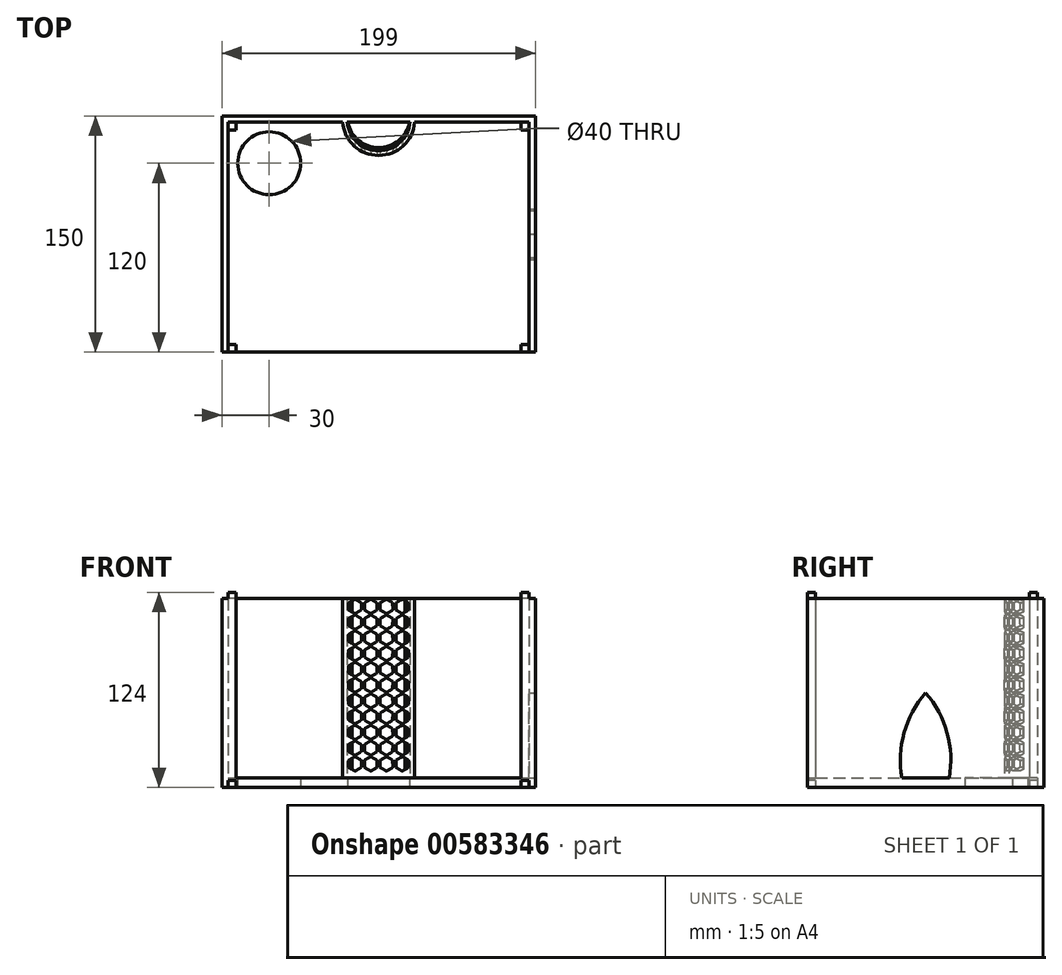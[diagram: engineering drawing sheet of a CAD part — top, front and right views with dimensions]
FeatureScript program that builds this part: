
annotation { "Feature Type Name" : "Feature", "Feature Type Description" : "" }
export const myFeature = defineFeature(function(context is Context, id is Id, definition is map)
    precondition{}
    {
        {
            var Q0;
            Q0=qCreatedBy(makeId("Top.planeOp"),FACE);
            var sketch = newSketch(context, id + "F0", { "sketchPlane" : qUnion([Q0])});
            skLineSegment(sketch, "E0.bottom", {"start": v(-99.5, 75) * mm, "end": v(99.5, 75) * mm});
            skLineSegment(sketch, "E0.left", {"start": v(-99.5, 75) * mm, "end": v(-99.5, -75) * mm});
            skLineSegment(sketch, "E0.right", {"start": v(99.5, 75) * mm, "end": v(99.5, -75) * mm});
            skPoint(sketch, "E0.middle", {"position": v(0, 0) * mm});
            skLineSegment(sketch, "E1.1", {"start": v(-95.5, 71) * mm, "end": v(-95.5, -70) * mm});
            skLineSegment(sketch, "E1.2", {"start": v(-95.5, 71) * mm, "end": v(95.4, 71) * mm});
            skLineSegment(sketch, "E1.3", {"start": v(95.4, 71) * mm, "end": v(95.4, -70) * mm});
            skLineSegment(sketch, "E2", {"start": v(0, -75) * mm, "end": v(0, -73) * mm});
            skPoint(sketch, "E2.endSnap0", {"position": v(0, -75) * mm});
            skPoint(sketch, "E3.end.orphan", {"position": v(95.5, 0) * mm});
            skLineSegment(sketch, "E4", {"start": v(-99.5, -75) * mm, "end": v(-95.5, -75) * mm});
            skLineSegment(sketch, "E5", {"start": v(-95.5, -75) * mm, "end": v(-95.5, -70) * mm});
            skLineSegment(sketch, "E6", {"start": v(95.4, -70) * mm, "end": v(95.4, -75) * mm});
            skLineSegment(sketch, "E7", {"start": v(95.4, -75) * mm, "end": v(99.5, -75) * mm});
            skPoint(sketch, "E8.end.orphan", {"position": v(-95.5, -70) * mm});
            skLineSegment(sketch, "E9", {"start": v(-90.5, 71) * mm, "end": v(-90.5, 66) * mm});
            skLineSegment(sketch, "E10", {"start": v(-90.5, 66) * mm, "end": v(-95.5, 66) * mm});
            skLineSegment(sketch, "E11", {"start": v(95.4, 66) * mm, "end": v(90.4, 66) * mm});
            skLineSegment(sketch, "E12", {"start": v(90.4, 66) * mm, "end": v(90.4, 71) * mm});
            skLineSegment(sketch, "E13", {"start": v(-95.5, 71) * mm, "end": v(-90.5, 71) * mm});
            skLineSegment(sketch, "E14", {"start": v(-95.5, 71) * mm, "end": v(-95.5, 66) * mm});
            skLineSegment(sketch, "E15", {"start": v(90.4, 71) * mm, "end": v(95.4, 71) * mm});
            skLineSegment(sketch, "E16", {"start": v(95.4, 66) * mm, "end": v(95.4, 71) * mm});
            skLineSegment(sketch, "E17", {"start": v(95.4, -75) * mm, "end": v(90.4, -75) * mm});
            skLineSegment(sketch, "E18", {"start": v(90.4, -75) * mm, "end": v(90.4, -70) * mm});
            skLineSegment(sketch, "E19", {"start": v(90.4, -70) * mm, "end": v(95.4, -70) * mm});
            skLineSegment(sketch, "E20", {"start": v(-95.5, -70) * mm, "end": v(-90.5, -70) * mm});
            skLineSegment(sketch, "E21", {"start": v(-95.5, -75) * mm, "end": v(-90.5, -75) * mm});
            skLineSegment(sketch, "E22", {"start": v(-90.5, -70) * mm, "end": v(-90.5, -75) * mm});
            skLineSegment(sketch, "E23", {"start": v(0, 73) * mm, "end": v(0, 71) * mm});
            skPoint(sketch, "E24.MirrorCS.end.orphan", {"position": v(-8.62, 71) * mm});
            skPoint(sketch, "E24.MirrorCS.start.orphan", {"position": v(8.62, 71) * mm});
            skArc(sketch, "E25", {"start": v(-19.9, 71) * mm, "mid": v(0, 53) * mm, "end": v(19.9, 71) * mm});
            skArc(sketch, "E26.0", {"start": v(-22.91, 71) * mm, "mid": v(0, 50) * mm, "end": v(22.91, 71) * mm});
            skSolve(sketch);
        }
        {
            var Q0;
            Q0=qCreatedBy(makeId("Top.planeOp"),FACE);
            var sketch = newSketch(context, id + "F1", { "sketchPlane" : qUnion([Q0])});
            skLineSegment(sketch, "E27.bottom", {"start": v(-99.5, 75) * mm, "end": v(-20, 75) * mm});
            skLineSegment(sketch, "E27.top", {"start": v(-99.5, -75) * mm, "end": v(99.5, -75) * mm});
            skLineSegment(sketch, "E27.left", {"start": v(-99.5, 75) * mm, "end": v(-99.5, -75) * mm});
            skLineSegment(sketch, "E27.right", {"start": v(99.5, 75) * mm, "end": v(99.5, -75) * mm});
            skPoint(sketch, "E27.middle", {"position": v(0, 0) * mm});
            skCircle(sketch, "E28", {"center": v(-69.5, 45) * mm, "radius": 20 * mm});
            skLineSegment(sketch, "E29.trimOffspring", {"start": v(20, 75) * mm, "end": v(99.5, 75) * mm});
            skArc(sketch, "E30", {"start": v(-20, 75) * mm, "mid": v(0, 55) * mm, "end": v(20, 75) * mm});
            skSolve(sketch);
        }
        {
            var Q0;
            Q0 = qSketchRegion(id + "F1", true);
            extrude(context, id + "F2", {"entities" : qUnion([Q0]), "depth" : 6 * mm, "offsetDistance" : 25 * mm});
        }
        {
            var Q0;
            Q0 = qSketchRegion(id + "F0", true);
            extrude(context, id + "F3", {"entities" : qUnion([Q0]), "operationType" : NewBodyOperationType.ADD, "depth" : 120 * mm, "offsetDistance" : 25 * mm});
        }
        {
            var Q0;
            Q0=makeQuery(id+"F0.imprint","IMPRINT",FACE,{"disambiguationData":[TD([[makeQuery(id+"F0.imprint","IMPRINT",EDGE,{"derivedFrom":sQuery(id+"F0.wireOp",EDGE,"E9")}),-1.0]])]});
            extrude(context, id + "F4", {"entities" : qUnion([Q0]), "operationType" : NewBodyOperationType.ADD, "depth" : 124 * mm, "offsetDistance" : 25 * mm});
        }
        {
            var Q0;
            Q0=makeQuery(id+"F0.imprint","IMPRINT",FACE,{"disambiguationData":[TD([[makeQuery(id+"F0.imprint","IMPRINT",EDGE,{"derivedFrom":sQuery(id+"F0.wireOp",EDGE,"E11")}),-1.0]])]});
            var Q1;
            Q1=makeQuery(id+"F0.imprint","IMPRINT",FACE,{"disambiguationData":[TD([[makeQuery(id+"F0.imprint","IMPRINT",EDGE,{"derivedFrom":sQuery(id+"F0.wireOp",EDGE,"E6")}),-1.0]])]});
            var Q2;
            Q2=makeQuery(id+"F0.imprint","IMPRINT",FACE,{"disambiguationData":[TD([[makeQuery(id+"F0.imprint","IMPRINT",EDGE,{"derivedFrom":sQuery(id+"F0.wireOp",EDGE,"E5")}),-1.0]])]});
            extrude(context, id + "F5", {"entities" : qUnion([Q0, Q1, Q2]), "operationType" : NewBodyOperationType.ADD, "depth" : 124 * mm, "offsetDistance" : 25 * mm});
        }
        {
            var Q0;
            Q0=makeQuery(id+"F3.boolean.opBoolean","MERGE",FACE,{"derivedFrom":[makeQuery(id+"F2.opExtrude","SWEPT_FACE",FACE,{"disambiguationData":[OSD([sQuery(id+"F1.wireOp",EDGE,"E27.right")])]}),makeQuery(id+"F3.opExtrude","SWEPT_FACE",FACE,{"disambiguationData":[OSD([sQuery(id+"F0.wireOp",EDGE,"E0.right")])]})]});
            var sketch = newSketch(context, id + "F6", { "sketchPlane" : qUnion([Q0])});
            skLineSegment(sketch, "E31", {"start": v(-15, 6) * mm, "end": v(0, 6) * mm});
            skLineSegment(sketch, "E32", {"start": v(15, 6) * mm, "end": v(0, 6) * mm});
            skArc(sketch, "E33", {"start": v(0, 60) * mm, "mid": v(-13.68, 34.72) * mm, "end": v(-15, 6) * mm});
            skArc(sketch, "E34.MirrorCS", {"start": v(0, 60) * mm, "mid": v(13.68, 34.72) * mm, "end": v(15, 6) * mm});
            skPoint(sketch, "E35.start.orphan", {"position": v(0, 0) * mm});
            skSolve(sketch);
        }
        {
            var Q0;
            Q0 = qSketchRegion(id + "F6", true);
            extrude(context, id + "F7", {"entities" : qUnion([Q0]), "operationType" : NewBodyOperationType.REMOVE, "oppositeDirection" : true, "depth" : 25 * mm, "offsetDistance" : 25 * mm});
        }
        {
            var Q0;
            Q0=makeQuery(id+"F0.imprint","IMPRINT",FACE,{"disambiguationData":[TD([[makeQuery(id+"F0.imprint","IMPRINT",EDGE,{"derivedFrom":sQuery(id+"F0.wireOp",EDGE,"E9")}),-1.0]])]});
            var Q1;
            Q1=makeQuery(id+"F0.imprint","IMPRINT",FACE,{"disambiguationData":[TD([[makeQuery(id+"F0.imprint","IMPRINT",EDGE,{"derivedFrom":sQuery(id+"F0.wireOp",EDGE,"E11")}),-1.0]])]});
            var Q2;
            Q2=makeQuery(id+"F0.imprint","IMPRINT",FACE,{"disambiguationData":[TD([[makeQuery(id+"F0.imprint","IMPRINT",EDGE,{"derivedFrom":sQuery(id+"F0.wireOp",EDGE,"E5")}),-1.0]])]});
            var Q3;
            Q3=makeQuery(id+"F0.imprint","IMPRINT",FACE,{"disambiguationData":[TD([[makeQuery(id+"F0.imprint","IMPRINT",EDGE,{"derivedFrom":sQuery(id+"F0.wireOp",EDGE,"E6")}),-1.0]])]});
            extrude(context, id + "F8", {"entities" : qUnion([Q0, Q1, Q2, Q3]), "operationType" : NewBodyOperationType.REMOVE, "depth" : 4.5 * mm, "offsetDistance" : 25 * mm});
        }
        {
            var Q0;
            Q0=makeQuery(id+"F0.imprint","IMPRINT",FACE,{"disambiguationData":[TD([[makeQuery(id+"F0.imprint","IMPRINT",EDGE,{"derivedFrom":sQuery(id+"F0.wireOp",EDGE,"E5")}),-1.0]])]});
            extrude(context, id + "F9", {"entities" : qUnion([Q0]), "operationType" : NewBodyOperationType.REMOVE, "depth" : 4.5 * mm, "offsetDistance" : 25 * mm});
        }
        {
            var Q0;
            Q0=qCreatedBy(makeId("Front.planeOp"),FACE);
            var sketch = newSketch(context, id + "F10", { "sketchPlane" : qUnion([Q0])});
            skLineSegment(sketch, "E36.top", {"start": v(-20, 0.02) * mm, "end": v(20, 0.02) * mm});
            skPoint(sketch, "E36.middle", {"position": v(0, 60.02) * mm});
            skPoint(sketch, "E37", {"position": v(-10, 115.02) * mm});
            skPoint(sketch, "E38", {"position": v(-15, 120.02) * mm});
            skLineSegment(sketch, "E39.0", {"start": v(-19.03, 117.28) * mm, "end": v(-15.05, 119.63) * mm});
            skLineSegment(sketch, "E39.1", {"start": v(-15.05, 119.63) * mm, "end": v(-11.03, 117.37) * mm});
            skLineSegment(sketch, "E39.2", {"start": v(-11.03, 117.37) * mm, "end": v(-10.97, 112.75) * mm});
            skLineSegment(sketch, "E39.3", {"start": v(-10.97, 112.75) * mm, "end": v(-14.95, 110.4) * mm});
            skLineSegment(sketch, "E39.4", {"start": v(-14.95, 110.4) * mm, "end": v(-18.97, 112.66) * mm});
            skLineSegment(sketch, "E39.5", {"start": v(-18.97, 112.66) * mm, "end": v(-19.03, 117.28) * mm});
            skPoint(sketch, "E39.0.midPoint", {"position": v(-17.04, 118.46) * mm});
            skCircle(sketch, "E40.MirrorC", {"center": v(-5, 115.02) * mm, "radius": 4 * mm, "construction": true});
            skLineSegment(sketch, "E41.MirrorCS", {"start": v(-0.97, 117.28) * mm, "end": v(-4.95, 119.63) * mm});
            skLineSegment(sketch, "E42.MirrorCS", {"start": v(-4.95, 119.63) * mm, "end": v(-8.97, 117.37) * mm});
            skLineSegment(sketch, "E43.MirrorCS", {"start": v(-8.97, 117.37) * mm, "end": v(-9.03, 112.75) * mm});
            skLineSegment(sketch, "E44.MirrorCS", {"start": v(-9.03, 112.75) * mm, "end": v(-5.05, 110.4) * mm});
            skLineSegment(sketch, "E45.MirrorCS", {"start": v(-5.05, 110.4) * mm, "end": v(-1.03, 112.66) * mm});
            skLineSegment(sketch, "E46.MirrorCS", {"start": v(-1.03, 112.66) * mm, "end": v(-0.97, 117.28) * mm});
            skLineSegment(sketch, "E47.MirrorCS", {"start": v(1.03, 112.66) * mm, "end": v(0.97, 117.28) * mm});
            skLineSegment(sketch, "E48.MirrorCS", {"start": v(0.97, 117.28) * mm, "end": v(4.95, 119.63) * mm});
            skLineSegment(sketch, "E49.MirrorCS", {"start": v(4.95, 119.63) * mm, "end": v(8.97, 117.37) * mm});
            skLineSegment(sketch, "E50.MirrorCS", {"start": v(8.97, 117.37) * mm, "end": v(9.03, 112.75) * mm});
            skLineSegment(sketch, "E51.MirrorCS", {"start": v(9.03, 112.75) * mm, "end": v(5.05, 110.4) * mm});
            skLineSegment(sketch, "E52.MirrorCS", {"start": v(5.05, 110.4) * mm, "end": v(1.03, 112.66) * mm});
            skLineSegment(sketch, "E53.MirrorCS", {"start": v(15.05, 119.63) * mm, "end": v(11.03, 117.37) * mm});
            skLineSegment(sketch, "E54.MirrorCS", {"start": v(11.03, 117.37) * mm, "end": v(10.97, 112.75) * mm});
            skLineSegment(sketch, "E55.MirrorCS", {"start": v(10.97, 112.75) * mm, "end": v(14.95, 110.4) * mm});
            skLineSegment(sketch, "E56.MirrorCS", {"start": v(14.95, 110.4) * mm, "end": v(18.97, 112.66) * mm});
            skLineSegment(sketch, "E57.MirrorCS", {"start": v(18.97, 112.66) * mm, "end": v(19.03, 117.28) * mm});
            skLineSegment(sketch, "E58.MirrorCS", {"start": v(19.03, 117.28) * mm, "end": v(15.05, 119.63) * mm});
            skLineSegment(sketch, "E59.MirrorCS", {"start": v(18.97, 107.37) * mm, "end": v(19.03, 102.75) * mm});
            skLineSegment(sketch, "E60.MirrorCS", {"start": v(19.03, 102.75) * mm, "end": v(15.05, 100.4) * mm});
            skLineSegment(sketch, "E61.MirrorCS", {"start": v(15.05, 100.4) * mm, "end": v(11.03, 102.66) * mm});
            skLineSegment(sketch, "E62.MirrorCS", {"start": v(11.03, 102.66) * mm, "end": v(10.97, 107.28) * mm});
            skLineSegment(sketch, "E63.MirrorCS", {"start": v(10.97, 107.28) * mm, "end": v(14.95, 109.63) * mm});
            skLineSegment(sketch, "E64.MirrorCS", {"start": v(14.95, 109.63) * mm, "end": v(18.97, 107.37) * mm});
            skLineSegment(sketch, "E65.MirrorCS", {"start": v(9.03, 107.28) * mm, "end": v(5.05, 109.63) * mm});
            skLineSegment(sketch, "E66.MirrorCS", {"start": v(5.05, 109.63) * mm, "end": v(1.03, 107.37) * mm});
            skLineSegment(sketch, "E67.MirrorCS", {"start": v(1.03, 107.37) * mm, "end": v(0.97, 102.75) * mm});
            skLineSegment(sketch, "E68.MirrorCS", {"start": v(0.97, 102.75) * mm, "end": v(4.95, 100.4) * mm});
            skLineSegment(sketch, "E69.MirrorCS", {"start": v(4.95, 100.4) * mm, "end": v(8.97, 102.66) * mm});
            skLineSegment(sketch, "E70.MirrorCS", {"start": v(8.97, 102.66) * mm, "end": v(9.03, 107.28) * mm});
            skLineSegment(sketch, "E71.MirrorCS", {"start": v(-8.97, 102.66) * mm, "end": v(-9.03, 107.28) * mm});
            skLineSegment(sketch, "E72.MirrorCS", {"start": v(-9.03, 107.28) * mm, "end": v(-5.05, 109.63) * mm});
            skLineSegment(sketch, "E73.MirrorCS", {"start": v(-5.05, 109.63) * mm, "end": v(-1.03, 107.37) * mm});
            skLineSegment(sketch, "E74.MirrorCS", {"start": v(-1.03, 107.37) * mm, "end": v(-0.97, 102.75) * mm});
            skLineSegment(sketch, "E75.MirrorCS", {"start": v(-0.97, 102.75) * mm, "end": v(-4.95, 100.4) * mm});
            skLineSegment(sketch, "E76.MirrorCS", {"start": v(-4.95, 100.4) * mm, "end": v(-8.97, 102.66) * mm});
            skLineSegment(sketch, "E77.MirrorCS", {"start": v(-10.97, 107.28) * mm, "end": v(-14.95, 109.63) * mm});
            skLineSegment(sketch, "E78.MirrorCS", {"start": v(-14.95, 109.63) * mm, "end": v(-18.97, 107.37) * mm});
            skLineSegment(sketch, "E79.MirrorCS", {"start": v(-18.97, 107.37) * mm, "end": v(-19.03, 102.75) * mm});
            skLineSegment(sketch, "E80.MirrorCS", {"start": v(-19.03, 102.75) * mm, "end": v(-15.05, 100.4) * mm});
            skLineSegment(sketch, "E81.MirrorCS", {"start": v(-15.05, 100.4) * mm, "end": v(-11.03, 102.66) * mm});
            skLineSegment(sketch, "E82.MirrorCS", {"start": v(-11.03, 102.66) * mm, "end": v(-10.97, 107.28) * mm});
            skLineSegment(sketch, "E83.MirrorCS", {"start": v(15.05, 99.63) * mm, "end": v(11.03, 97.37) * mm});
            skLineSegment(sketch, "E84.MirrorCS", {"start": v(11.03, 97.37) * mm, "end": v(10.97, 92.75) * mm});
            skLineSegment(sketch, "E85.MirrorCS", {"start": v(10.97, 92.75) * mm, "end": v(14.95, 90.4) * mm});
            skLineSegment(sketch, "E86.MirrorCS", {"start": v(14.95, 90.4) * mm, "end": v(18.97, 92.66) * mm});
            skLineSegment(sketch, "E87.MirrorCS", {"start": v(18.97, 92.66) * mm, "end": v(19.03, 97.28) * mm});
            skLineSegment(sketch, "E88.MirrorCS", {"start": v(19.03, 97.28) * mm, "end": v(15.05, 99.63) * mm});
            skLineSegment(sketch, "E89.MirrorCS", {"start": v(8.97, 97.37) * mm, "end": v(9.03, 92.75) * mm});
            skLineSegment(sketch, "E90.MirrorCS", {"start": v(9.03, 92.75) * mm, "end": v(5.05, 90.4) * mm});
            skLineSegment(sketch, "E91.MirrorCS", {"start": v(5.05, 90.4) * mm, "end": v(1.03, 92.66) * mm});
            skLineSegment(sketch, "E92.MirrorCS", {"start": v(1.03, 92.66) * mm, "end": v(0.97, 97.28) * mm});
            skLineSegment(sketch, "E93.MirrorCS", {"start": v(0.97, 97.28) * mm, "end": v(4.95, 99.63) * mm});
            skLineSegment(sketch, "E94.MirrorCS", {"start": v(4.95, 99.63) * mm, "end": v(8.97, 97.37) * mm});
            skLineSegment(sketch, "E95.MirrorCS", {"start": v(-1.03, 92.66) * mm, "end": v(-0.97, 97.28) * mm});
            skLineSegment(sketch, "E96.MirrorCS", {"start": v(-5.05, 90.4) * mm, "end": v(-1.03, 92.66) * mm});
            skLineSegment(sketch, "E97.MirrorCS", {"start": v(-9.03, 92.75) * mm, "end": v(-5.05, 90.4) * mm});
            skLineSegment(sketch, "E98.MirrorCS", {"start": v(-4.95, 99.63) * mm, "end": v(-8.97, 97.37) * mm});
            skLineSegment(sketch, "E99.MirrorCS", {"start": v(-0.97, 97.28) * mm, "end": v(-4.95, 99.63) * mm});
            skLineSegment(sketch, "E100.MirrorCS", {"start": v(-11.03, 97.37) * mm, "end": v(-10.97, 92.75) * mm});
            skLineSegment(sketch, "E101.MirrorCS", {"start": v(-15.05, 99.63) * mm, "end": v(-11.03, 97.37) * mm});
            skLineSegment(sketch, "E102.MirrorCS", {"start": v(-19.03, 97.28) * mm, "end": v(-15.05, 99.63) * mm});
            skLineSegment(sketch, "E103.MirrorCS", {"start": v(-18.97, 92.66) * mm, "end": v(-19.03, 97.28) * mm});
            skLineSegment(sketch, "E104.MirrorCS", {"start": v(-14.95, 90.4) * mm, "end": v(-18.97, 92.66) * mm});
            skLineSegment(sketch, "E105.MirrorCS", {"start": v(-10.97, 92.75) * mm, "end": v(-14.95, 90.4) * mm});
            skLineSegment(sketch, "E106.MirrorCS", {"start": v(-8.97, 97.37) * mm, "end": v(-9.03, 92.75) * mm});
            skLineSegment(sketch, "E107.MirrorCS", {"start": v(18.97, 87.37) * mm, "end": v(19.03, 82.75) * mm});
            skLineSegment(sketch, "E108.MirrorCS", {"start": v(19.03, 82.75) * mm, "end": v(15.05, 80.4) * mm});
            skLineSegment(sketch, "E109.MirrorCS", {"start": v(15.05, 80.4) * mm, "end": v(11.03, 82.66) * mm});
            skLineSegment(sketch, "E110.MirrorCS", {"start": v(11.03, 82.66) * mm, "end": v(10.97, 87.28) * mm});
            skLineSegment(sketch, "E111.MirrorCS", {"start": v(10.97, 87.28) * mm, "end": v(14.95, 89.63) * mm});
            skLineSegment(sketch, "E112.MirrorCS", {"start": v(14.95, 89.63) * mm, "end": v(18.97, 87.37) * mm});
            skLineSegment(sketch, "E113.MirrorCS", {"start": v(8.97, 82.66) * mm, "end": v(9.03, 87.28) * mm});
            skLineSegment(sketch, "E114.MirrorCS", {"start": v(4.95, 80.4) * mm, "end": v(8.97, 82.66) * mm});
            skLineSegment(sketch, "E115.MirrorCS", {"start": v(0.97, 82.75) * mm, "end": v(4.95, 80.4) * mm});
            skLineSegment(sketch, "E116.MirrorCS", {"start": v(1.03, 87.37) * mm, "end": v(0.97, 82.75) * mm});
            skLineSegment(sketch, "E117.MirrorCS", {"start": v(5.05, 89.63) * mm, "end": v(1.03, 87.37) * mm});
            skLineSegment(sketch, "E118.MirrorCS", {"start": v(9.03, 87.28) * mm, "end": v(5.05, 89.63) * mm});
            skLineSegment(sketch, "E119.MirrorCS", {"start": v(-1.03, 87.37) * mm, "end": v(-0.97, 82.75) * mm});
            skLineSegment(sketch, "E120.MirrorCS", {"start": v(-0.97, 82.75) * mm, "end": v(-4.95, 80.4) * mm});
            skLineSegment(sketch, "E121.MirrorCS", {"start": v(-4.95, 80.4) * mm, "end": v(-8.97, 82.66) * mm});
            skLineSegment(sketch, "E122.MirrorCS", {"start": v(-8.97, 82.66) * mm, "end": v(-9.03, 87.28) * mm});
            skLineSegment(sketch, "E123.MirrorCS", {"start": v(-9.03, 87.28) * mm, "end": v(-5.05, 89.63) * mm});
            skLineSegment(sketch, "E124.MirrorCS", {"start": v(-5.05, 89.63) * mm, "end": v(-1.03, 87.37) * mm});
            skLineSegment(sketch, "E125.MirrorCS", {"start": v(-11.03, 82.66) * mm, "end": v(-10.97, 87.28) * mm});
            skLineSegment(sketch, "E126.MirrorCS", {"start": v(-15.05, 80.4) * mm, "end": v(-11.03, 82.66) * mm});
            skLineSegment(sketch, "E127.MirrorCS", {"start": v(-19.03, 82.75) * mm, "end": v(-15.05, 80.4) * mm});
            skLineSegment(sketch, "E128.MirrorCS", {"start": v(-18.97, 87.37) * mm, "end": v(-19.03, 82.75) * mm});
            skLineSegment(sketch, "E129.MirrorCS", {"start": v(-14.95, 89.63) * mm, "end": v(-18.97, 87.37) * mm});
            skLineSegment(sketch, "E130.MirrorCS", {"start": v(-10.97, 87.28) * mm, "end": v(-14.95, 89.63) * mm});
            skLineSegment(sketch, "E131.MirrorCS", {"start": v(-4.95, 79.63) * mm, "end": v(-8.97, 77.37) * mm});
            skLineSegment(sketch, "E132.MirrorCS", {"start": v(-8.97, 77.37) * mm, "end": v(-9.03, 72.75) * mm});
            skLineSegment(sketch, "E133.MirrorCS", {"start": v(-9.03, 72.75) * mm, "end": v(-5.05, 70.4) * mm});
            skLineSegment(sketch, "E134.MirrorCS", {"start": v(-5.05, 70.4) * mm, "end": v(-1.03, 72.66) * mm});
            skLineSegment(sketch, "E135.MirrorCS", {"start": v(-1.03, 72.66) * mm, "end": v(-0.97, 77.28) * mm});
            skLineSegment(sketch, "E136.MirrorCS", {"start": v(-0.97, 77.28) * mm, "end": v(-4.95, 79.63) * mm});
            skLineSegment(sketch, "E137.MirrorCS", {"start": v(1.03, 72.66) * mm, "end": v(0.97, 77.28) * mm});
            skLineSegment(sketch, "E138.MirrorCS", {"start": v(5.05, 70.4) * mm, "end": v(1.03, 72.66) * mm});
            skLineSegment(sketch, "E139.MirrorCS", {"start": v(9.03, 72.75) * mm, "end": v(5.05, 70.4) * mm});
            skLineSegment(sketch, "E140.MirrorCS", {"start": v(8.97, 77.37) * mm, "end": v(9.03, 72.75) * mm});
            skLineSegment(sketch, "E141.MirrorCS", {"start": v(4.95, 79.63) * mm, "end": v(8.97, 77.37) * mm});
            skLineSegment(sketch, "E142.MirrorCS", {"start": v(0.97, 77.28) * mm, "end": v(4.95, 79.63) * mm});
            skLineSegment(sketch, "E143.MirrorCS", {"start": v(11.03, 77.37) * mm, "end": v(10.97, 72.75) * mm});
            skLineSegment(sketch, "E144.MirrorCS", {"start": v(10.97, 72.75) * mm, "end": v(14.95, 70.4) * mm});
            skLineSegment(sketch, "E145.MirrorCS", {"start": v(14.95, 70.4) * mm, "end": v(18.97, 72.66) * mm});
            skLineSegment(sketch, "E146.MirrorCS", {"start": v(18.97, 72.66) * mm, "end": v(19.03, 77.28) * mm});
            skLineSegment(sketch, "E147.MirrorCS", {"start": v(19.03, 77.28) * mm, "end": v(15.05, 79.63) * mm});
            skLineSegment(sketch, "E148.MirrorCS", {"start": v(15.05, 79.63) * mm, "end": v(11.03, 77.37) * mm});
            skLineSegment(sketch, "E149.MirrorCS", {"start": v(-11.03, 77.37) * mm, "end": v(-10.97, 72.75) * mm});
            skLineSegment(sketch, "E150.MirrorCS", {"start": v(-10.97, 72.75) * mm, "end": v(-14.95, 70.4) * mm});
            skLineSegment(sketch, "E151.MirrorCS", {"start": v(-14.95, 70.4) * mm, "end": v(-18.97, 72.66) * mm});
            skLineSegment(sketch, "E152.MirrorCS", {"start": v(-18.97, 72.66) * mm, "end": v(-19.03, 77.28) * mm});
            skLineSegment(sketch, "E153.MirrorCS", {"start": v(-19.03, 77.28) * mm, "end": v(-15.05, 79.63) * mm});
            skLineSegment(sketch, "E154.MirrorCS", {"start": v(-15.05, 79.63) * mm, "end": v(-11.03, 77.37) * mm});
            skLineSegment(sketch, "E155.MirrorCS", {"start": v(10.97, 67.28) * mm, "end": v(14.95, 69.63) * mm});
            skLineSegment(sketch, "E156.MirrorCS", {"start": v(11.03, 62.66) * mm, "end": v(10.97, 67.28) * mm});
            skLineSegment(sketch, "E157.MirrorCS", {"start": v(15.05, 60.4) * mm, "end": v(11.03, 62.66) * mm});
            skLineSegment(sketch, "E158.MirrorCS", {"start": v(19.03, 62.75) * mm, "end": v(15.05, 60.4) * mm});
            skLineSegment(sketch, "E159.MirrorCS", {"start": v(18.97, 67.37) * mm, "end": v(19.03, 62.75) * mm});
            skLineSegment(sketch, "E160.MirrorCS", {"start": v(14.95, 69.63) * mm, "end": v(18.97, 67.37) * mm});
            skLineSegment(sketch, "E161.MirrorCS", {"start": v(8.97, 62.66) * mm, "end": v(9.03, 67.28) * mm});
            skLineSegment(sketch, "E162.MirrorCS", {"start": v(4.95, 60.4) * mm, "end": v(8.97, 62.66) * mm});
            skLineSegment(sketch, "E163.MirrorCS", {"start": v(0.97, 62.75) * mm, "end": v(4.95, 60.4) * mm});
            skLineSegment(sketch, "E164.MirrorCS", {"start": v(1.03, 67.37) * mm, "end": v(0.97, 62.75) * mm});
            skLineSegment(sketch, "E165.MirrorCS", {"start": v(5.05, 69.63) * mm, "end": v(1.03, 67.37) * mm});
            skLineSegment(sketch, "E166.MirrorCS", {"start": v(9.03, 67.28) * mm, "end": v(5.05, 69.63) * mm});
            skLineSegment(sketch, "E167.MirrorCS", {"start": v(-1.03, 67.37) * mm, "end": v(-0.97, 62.75) * mm});
            skLineSegment(sketch, "E168.MirrorCS", {"start": v(-0.97, 62.75) * mm, "end": v(-4.95, 60.4) * mm});
            skLineSegment(sketch, "E169.MirrorCS", {"start": v(-4.95, 60.4) * mm, "end": v(-8.97, 62.66) * mm});
            skLineSegment(sketch, "E170.MirrorCS", {"start": v(-8.97, 62.66) * mm, "end": v(-9.03, 67.28) * mm});
            skLineSegment(sketch, "E171.MirrorCS", {"start": v(-9.03, 67.28) * mm, "end": v(-5.05, 69.63) * mm});
            skLineSegment(sketch, "E172.MirrorCS", {"start": v(-5.05, 69.63) * mm, "end": v(-1.03, 67.37) * mm});
            skLineSegment(sketch, "E173.MirrorCS", {"start": v(-11.03, 62.66) * mm, "end": v(-10.97, 67.28) * mm});
            skLineSegment(sketch, "E174.MirrorCS", {"start": v(-15.05, 60.4) * mm, "end": v(-11.03, 62.66) * mm});
            skLineSegment(sketch, "E175.MirrorCS", {"start": v(-19.03, 62.75) * mm, "end": v(-15.05, 60.4) * mm});
            skLineSegment(sketch, "E176.MirrorCS", {"start": v(-18.97, 67.37) * mm, "end": v(-19.03, 62.75) * mm});
            skLineSegment(sketch, "E177.MirrorCS", {"start": v(-14.95, 69.63) * mm, "end": v(-18.97, 67.37) * mm});
            skLineSegment(sketch, "E178.MirrorCS", {"start": v(-10.97, 67.28) * mm, "end": v(-14.95, 69.63) * mm});
            skLineSegment(sketch, "E179.MirrorCS", {"start": v(15.05, 59.63) * mm, "end": v(11.03, 57.37) * mm});
            skLineSegment(sketch, "E180.MirrorCS", {"start": v(11.03, 57.37) * mm, "end": v(10.97, 52.75) * mm});
            skLineSegment(sketch, "E181.MirrorCS", {"start": v(19.03, 57.28) * mm, "end": v(15.05, 59.63) * mm});
            skLineSegment(sketch, "E182.MirrorCS", {"start": v(18.97, 52.66) * mm, "end": v(19.03, 57.28) * mm});
            skLineSegment(sketch, "E183.MirrorCS", {"start": v(14.95, 50.4) * mm, "end": v(18.97, 52.66) * mm});
            skLineSegment(sketch, "E184.MirrorCS", {"start": v(10.97, 52.75) * mm, "end": v(14.95, 50.4) * mm});
            skLineSegment(sketch, "E185.MirrorCS", {"start": v(8.97, 57.37) * mm, "end": v(9.03, 52.75) * mm});
            skLineSegment(sketch, "E186.MirrorCS", {"start": v(9.03, 52.75) * mm, "end": v(5.05, 50.4) * mm});
            skLineSegment(sketch, "E187.MirrorCS", {"start": v(5.05, 50.4) * mm, "end": v(1.03, 52.66) * mm});
            skLineSegment(sketch, "E188.MirrorCS", {"start": v(1.03, 52.66) * mm, "end": v(0.97, 57.28) * mm});
            skLineSegment(sketch, "E189.MirrorCS", {"start": v(0.97, 57.28) * mm, "end": v(4.95, 59.63) * mm});
            skLineSegment(sketch, "E190.MirrorCS", {"start": v(4.95, 59.63) * mm, "end": v(8.97, 57.37) * mm});
            skLineSegment(sketch, "E191.MirrorCS", {"start": v(-1.03, 52.66) * mm, "end": v(-0.97, 57.28) * mm});
            skLineSegment(sketch, "E192.MirrorCS", {"start": v(-5.05, 50.4) * mm, "end": v(-1.03, 52.66) * mm});
            skLineSegment(sketch, "E193.MirrorCS", {"start": v(-9.03, 52.75) * mm, "end": v(-5.05, 50.4) * mm});
            skLineSegment(sketch, "E194.MirrorCS", {"start": v(-8.97, 57.37) * mm, "end": v(-9.03, 52.75) * mm});
            skLineSegment(sketch, "E195.MirrorCS", {"start": v(-4.95, 59.63) * mm, "end": v(-8.97, 57.37) * mm});
            skLineSegment(sketch, "E196.MirrorCS", {"start": v(-0.97, 57.28) * mm, "end": v(-4.95, 59.63) * mm});
            skLineSegment(sketch, "E197.MirrorCS", {"start": v(-11.03, 57.37) * mm, "end": v(-10.97, 52.75) * mm});
            skLineSegment(sketch, "E198.MirrorCS", {"start": v(-10.97, 52.75) * mm, "end": v(-14.95, 50.4) * mm});
            skLineSegment(sketch, "E199.MirrorCS", {"start": v(-14.95, 50.4) * mm, "end": v(-18.97, 52.66) * mm});
            skLineSegment(sketch, "E200.MirrorCS", {"start": v(-18.97, 52.66) * mm, "end": v(-19.03, 57.28) * mm});
            skLineSegment(sketch, "E201.MirrorCS", {"start": v(-19.03, 57.28) * mm, "end": v(-15.05, 59.63) * mm});
            skLineSegment(sketch, "E202.MirrorCS", {"start": v(-15.05, 59.63) * mm, "end": v(-11.03, 57.37) * mm});
            skLineSegment(sketch, "E203.MirrorCS", {"start": v(11.03, 42.66) * mm, "end": v(10.97, 47.28) * mm});
            skLineSegment(sketch, "E204.MirrorCS", {"start": v(15.05, 40.4) * mm, "end": v(11.03, 42.66) * mm});
            skLineSegment(sketch, "E205.MirrorCS", {"start": v(19.03, 42.75) * mm, "end": v(15.05, 40.4) * mm});
            skLineSegment(sketch, "E206.MirrorCS", {"start": v(18.97, 47.37) * mm, "end": v(19.03, 42.75) * mm});
            skLineSegment(sketch, "E207.MirrorCS", {"start": v(14.95, 49.63) * mm, "end": v(18.97, 47.37) * mm});
            skLineSegment(sketch, "E208.MirrorCS", {"start": v(10.97, 47.28) * mm, "end": v(14.95, 49.63) * mm});
            skLineSegment(sketch, "E209.MirrorCS", {"start": v(8.97, 42.66) * mm, "end": v(9.03, 47.28) * mm});
            skLineSegment(sketch, "E210.MirrorCS", {"start": v(4.95, 40.4) * mm, "end": v(8.97, 42.66) * mm});
            skLineSegment(sketch, "E211.MirrorCS", {"start": v(0.97, 42.75) * mm, "end": v(4.95, 40.4) * mm});
            skLineSegment(sketch, "E212.MirrorCS", {"start": v(1.03, 47.37) * mm, "end": v(0.97, 42.75) * mm});
            skLineSegment(sketch, "E213.MirrorCS", {"start": v(5.05, 49.63) * mm, "end": v(1.03, 47.37) * mm});
            skLineSegment(sketch, "E214.MirrorCS", {"start": v(9.03, 47.28) * mm, "end": v(5.05, 49.63) * mm});
            skLineSegment(sketch, "E215.MirrorCS", {"start": v(-1.03, 47.37) * mm, "end": v(-0.97, 42.75) * mm});
            skLineSegment(sketch, "E216.MirrorCS", {"start": v(-0.97, 42.75) * mm, "end": v(-4.95, 40.4) * mm});
            skLineSegment(sketch, "E217.MirrorCS", {"start": v(-4.95, 40.4) * mm, "end": v(-8.97, 42.66) * mm});
            skLineSegment(sketch, "E218.MirrorCS", {"start": v(-8.97, 42.66) * mm, "end": v(-9.03, 47.28) * mm});
            skLineSegment(sketch, "E219.MirrorCS", {"start": v(-9.03, 47.28) * mm, "end": v(-5.05, 49.63) * mm});
            skLineSegment(sketch, "E220.MirrorCS", {"start": v(-5.05, 49.63) * mm, "end": v(-1.03, 47.37) * mm});
            skLineSegment(sketch, "E221.MirrorCS", {"start": v(-11.03, 42.66) * mm, "end": v(-10.97, 47.28) * mm});
            skLineSegment(sketch, "E222.MirrorCS", {"start": v(-15.05, 40.4) * mm, "end": v(-11.03, 42.66) * mm});
            skLineSegment(sketch, "E223.MirrorCS", {"start": v(-19.03, 42.75) * mm, "end": v(-15.05, 40.4) * mm});
            skLineSegment(sketch, "E224.MirrorCS", {"start": v(-18.97, 47.37) * mm, "end": v(-19.03, 42.75) * mm});
            skLineSegment(sketch, "E225.MirrorCS", {"start": v(-14.95, 49.63) * mm, "end": v(-18.97, 47.37) * mm});
            skLineSegment(sketch, "E226.MirrorCS", {"start": v(-10.97, 47.28) * mm, "end": v(-14.95, 49.63) * mm});
            skLineSegment(sketch, "E227.MirrorCS", {"start": v(19.03, 37.28) * mm, "end": v(15.05, 39.63) * mm});
            skLineSegment(sketch, "E228.MirrorCS", {"start": v(18.97, 32.66) * mm, "end": v(19.03, 37.28) * mm});
            skLineSegment(sketch, "E229.MirrorCS", {"start": v(14.95, 30.4) * mm, "end": v(18.97, 32.66) * mm});
            skLineSegment(sketch, "E230.MirrorCS", {"start": v(10.97, 32.75) * mm, "end": v(14.95, 30.4) * mm});
            skLineSegment(sketch, "E231.MirrorCS", {"start": v(11.03, 37.37) * mm, "end": v(10.97, 32.75) * mm});
            skLineSegment(sketch, "E232.MirrorCS", {"start": v(15.05, 39.63) * mm, "end": v(11.03, 37.37) * mm});
            skLineSegment(sketch, "E233.MirrorCS", {"start": v(8.97, 37.37) * mm, "end": v(9.03, 32.75) * mm});
            skLineSegment(sketch, "E234.MirrorCS", {"start": v(9.03, 32.75) * mm, "end": v(5.05, 30.4) * mm});
            skLineSegment(sketch, "E235.MirrorCS", {"start": v(5.05, 30.4) * mm, "end": v(1.03, 32.66) * mm});
            skLineSegment(sketch, "E236.MirrorCS", {"start": v(1.03, 32.66) * mm, "end": v(0.97, 37.28) * mm});
            skLineSegment(sketch, "E237.MirrorCS", {"start": v(0.97, 37.28) * mm, "end": v(4.95, 39.63) * mm});
            skLineSegment(sketch, "E238.MirrorCS", {"start": v(4.95, 39.63) * mm, "end": v(8.97, 37.37) * mm});
            skLineSegment(sketch, "E239.MirrorCS", {"start": v(-1.03, 32.66) * mm, "end": v(-0.97, 37.28) * mm});
            skLineSegment(sketch, "E240.MirrorCS", {"start": v(-5.05, 30.4) * mm, "end": v(-1.03, 32.66) * mm});
            skLineSegment(sketch, "E241.MirrorCS", {"start": v(-9.03, 32.75) * mm, "end": v(-5.05, 30.4) * mm});
            skLineSegment(sketch, "E242.MirrorCS", {"start": v(-8.97, 37.37) * mm, "end": v(-9.03, 32.75) * mm});
            skLineSegment(sketch, "E243.MirrorCS", {"start": v(-4.95, 39.63) * mm, "end": v(-8.97, 37.37) * mm});
            skLineSegment(sketch, "E244.MirrorCS", {"start": v(-0.97, 37.28) * mm, "end": v(-4.95, 39.63) * mm});
            skLineSegment(sketch, "E245.MirrorCS", {"start": v(-11.03, 37.37) * mm, "end": v(-10.97, 32.75) * mm});
            skLineSegment(sketch, "E246.MirrorCS", {"start": v(-10.97, 32.75) * mm, "end": v(-14.95, 30.4) * mm});
            skLineSegment(sketch, "E247.MirrorCS", {"start": v(-14.95, 30.4) * mm, "end": v(-18.97, 32.66) * mm});
            skLineSegment(sketch, "E248.MirrorCS", {"start": v(-18.97, 32.66) * mm, "end": v(-19.03, 37.28) * mm});
            skLineSegment(sketch, "E249.MirrorCS", {"start": v(-19.03, 37.28) * mm, "end": v(-15.05, 39.63) * mm});
            skLineSegment(sketch, "E250.MirrorCS", {"start": v(-15.05, 39.63) * mm, "end": v(-11.03, 37.37) * mm});
            skLineSegment(sketch, "E251.MirrorCS", {"start": v(10.97, 27.28) * mm, "end": v(14.95, 29.63) * mm});
            skLineSegment(sketch, "E252.MirrorCS", {"start": v(11.03, 22.66) * mm, "end": v(10.97, 27.28) * mm});
            skLineSegment(sketch, "E253.MirrorCS", {"start": v(15.05, 20.4) * mm, "end": v(11.03, 22.66) * mm});
            skLineSegment(sketch, "E254.MirrorCS", {"start": v(19.03, 22.75) * mm, "end": v(15.05, 20.4) * mm});
            skLineSegment(sketch, "E255.MirrorCS", {"start": v(18.97, 27.37) * mm, "end": v(19.03, 22.75) * mm});
            skLineSegment(sketch, "E256.MirrorCS", {"start": v(14.95, 29.63) * mm, "end": v(18.97, 27.37) * mm});
            skLineSegment(sketch, "E257.MirrorCS", {"start": v(8.97, 22.66) * mm, "end": v(9.03, 27.28) * mm});
            skLineSegment(sketch, "E258.MirrorCS", {"start": v(4.95, 20.4) * mm, "end": v(8.97, 22.66) * mm});
            skLineSegment(sketch, "E259.MirrorCS", {"start": v(0.97, 22.75) * mm, "end": v(4.95, 20.4) * mm});
            skLineSegment(sketch, "E260.MirrorCS", {"start": v(1.03, 27.37) * mm, "end": v(0.97, 22.75) * mm});
            skLineSegment(sketch, "E261.MirrorCS", {"start": v(5.05, 29.63) * mm, "end": v(1.03, 27.37) * mm});
            skLineSegment(sketch, "E262.MirrorCS", {"start": v(9.03, 27.28) * mm, "end": v(5.05, 29.63) * mm});
            skLineSegment(sketch, "E263.MirrorCS", {"start": v(-1.03, 27.37) * mm, "end": v(-0.97, 22.75) * mm});
            skLineSegment(sketch, "E264.MirrorCS", {"start": v(-0.97, 22.75) * mm, "end": v(-4.95, 20.4) * mm});
            skLineSegment(sketch, "E265.MirrorCS", {"start": v(-4.95, 20.4) * mm, "end": v(-8.97, 22.66) * mm});
            skLineSegment(sketch, "E266.MirrorCS", {"start": v(-8.97, 22.66) * mm, "end": v(-9.03, 27.28) * mm});
            skLineSegment(sketch, "E267.MirrorCS", {"start": v(-9.03, 27.28) * mm, "end": v(-5.05, 29.63) * mm});
            skLineSegment(sketch, "E268.MirrorCS", {"start": v(-5.05, 29.63) * mm, "end": v(-1.03, 27.37) * mm});
            skLineSegment(sketch, "E269.MirrorCS", {"start": v(-11.03, 22.66) * mm, "end": v(-10.97, 27.28) * mm});
            skLineSegment(sketch, "E270.MirrorCS", {"start": v(-15.05, 20.4) * mm, "end": v(-11.03, 22.66) * mm});
            skLineSegment(sketch, "E271.MirrorCS", {"start": v(-19.03, 22.75) * mm, "end": v(-15.05, 20.4) * mm});
            skLineSegment(sketch, "E272.MirrorCS", {"start": v(-18.97, 27.37) * mm, "end": v(-19.03, 22.75) * mm});
            skLineSegment(sketch, "E273.MirrorCS", {"start": v(-14.95, 29.63) * mm, "end": v(-18.97, 27.37) * mm});
            skLineSegment(sketch, "E274.MirrorCS", {"start": v(-10.97, 27.28) * mm, "end": v(-14.95, 29.63) * mm});
            skLineSegment(sketch, "E275.MirrorCS", {"start": v(19.03, 17.28) * mm, "end": v(15.05, 19.63) * mm});
            skLineSegment(sketch, "E276.MirrorCS", {"start": v(18.97, 12.66) * mm, "end": v(19.03, 17.28) * mm});
            skLineSegment(sketch, "E277.MirrorCS", {"start": v(14.95, 10.4) * mm, "end": v(18.97, 12.66) * mm});
            skLineSegment(sketch, "E278.MirrorCS", {"start": v(10.97, 12.75) * mm, "end": v(14.95, 10.4) * mm});
            skLineSegment(sketch, "E279.MirrorCS", {"start": v(11.03, 17.37) * mm, "end": v(10.97, 12.75) * mm});
            skLineSegment(sketch, "E280.MirrorCS", {"start": v(15.05, 19.63) * mm, "end": v(11.03, 17.37) * mm});
            skLineSegment(sketch, "E281.MirrorCS", {"start": v(8.97, 17.37) * mm, "end": v(9.03, 12.75) * mm});
            skLineSegment(sketch, "E282.MirrorCS", {"start": v(9.03, 12.75) * mm, "end": v(5.05, 10.4) * mm});
            skLineSegment(sketch, "E283.MirrorCS", {"start": v(5.05, 10.4) * mm, "end": v(1.03, 12.66) * mm});
            skLineSegment(sketch, "E284.MirrorCS", {"start": v(1.03, 12.66) * mm, "end": v(0.97, 17.28) * mm});
            skLineSegment(sketch, "E285.MirrorCS", {"start": v(4.95, 19.63) * mm, "end": v(8.97, 17.37) * mm});
            skLineSegment(sketch, "E286.MirrorCS", {"start": v(-9.03, 12.75) * mm, "end": v(-5.05, 10.4) * mm});
            skLineSegment(sketch, "E287.MirrorCS", {"start": v(-8.97, 17.37) * mm, "end": v(-9.03, 12.75) * mm});
            skLineSegment(sketch, "E288.MirrorCS", {"start": v(-4.95, 19.63) * mm, "end": v(-8.97, 17.37) * mm});
            skLineSegment(sketch, "E289.MirrorCS", {"start": v(-0.97, 17.28) * mm, "end": v(-4.95, 19.63) * mm});
            skLineSegment(sketch, "E290.MirrorCS", {"start": v(-11.03, 17.37) * mm, "end": v(-10.97, 12.75) * mm});
            skLineSegment(sketch, "E291.MirrorCS", {"start": v(-10.97, 12.75) * mm, "end": v(-14.95, 10.4) * mm});
            skLineSegment(sketch, "E292.MirrorCS", {"start": v(-14.95, 10.4) * mm, "end": v(-18.97, 12.66) * mm});
            skLineSegment(sketch, "E293.MirrorCS", {"start": v(-18.97, 12.66) * mm, "end": v(-19.03, 17.28) * mm});
            skLineSegment(sketch, "E294.MirrorCS", {"start": v(-19.03, 17.28) * mm, "end": v(-15.05, 19.63) * mm});
            skLineSegment(sketch, "E295.MirrorCS", {"start": v(-15.05, 19.63) * mm, "end": v(-11.03, 17.37) * mm});
            skLineSegment(sketch, "E296.MirrorCS", {"start": v(0.97, 17.28) * mm, "end": v(4.95, 19.63) * mm});
            skLineSegment(sketch, "E297.MirrorCS", {"start": v(-1.03, 12.66) * mm, "end": v(-0.97, 17.28) * mm});
            skLineSegment(sketch, "E298.MirrorCS", {"start": v(-5.05, 10.4) * mm, "end": v(-1.03, 12.66) * mm});
            skSolve(sketch);
        }
        {
            var Q0;
            Q0 = qSketchRegion(id + "F10", true);
            extrude(context, id + "F11", {"entities" : qUnion([Q0]), "operationType" : NewBodyOperationType.REMOVE, "oppositeDirection" : true, "depth" : 62.2 * mm, "offsetDistance" : 25 * mm});
        }
    });
